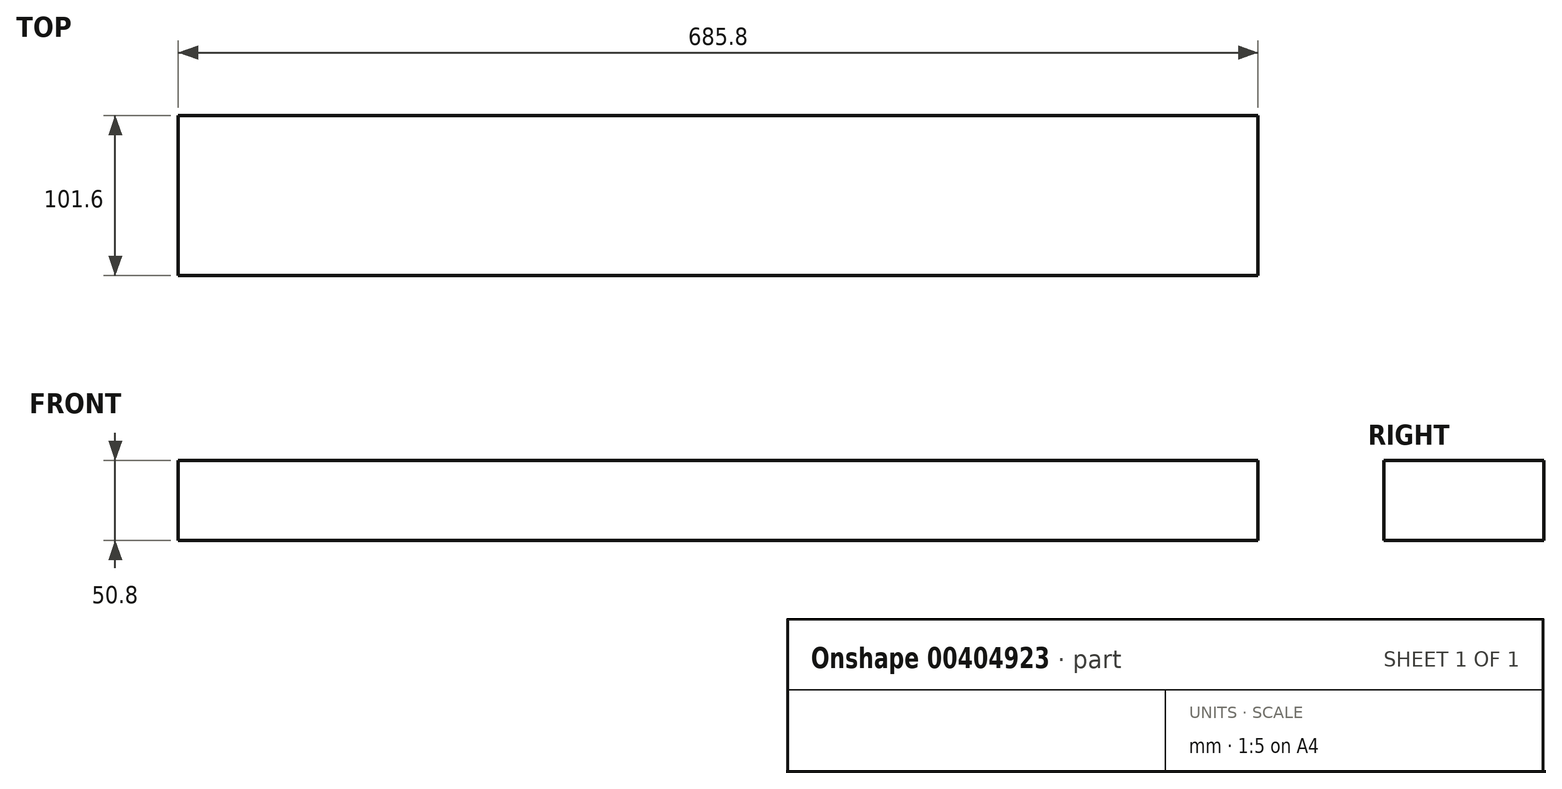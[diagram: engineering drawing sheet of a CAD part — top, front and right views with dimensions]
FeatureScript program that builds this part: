
annotation { "Feature Type Name" : "Feature", "Feature Type Description" : "" }
export const myFeature = defineFeature(function(context is Context, id is Id, definition is map)
    precondition{}
    {
        {
            var Q0;
            Q0=qCreatedBy(makeId("Right.planeOp"),FACE);
            var sketch = newSketch(context, id + "F0", { "sketchPlane" : qUnion([Q0])});
            skLineSegment(sketch, "E0.bottom", {"start": v(0, 0) * mm, "end": v(101.6, 0) * mm});
            skLineSegment(sketch, "E0.top", {"start": v(0, 50.8) * mm, "end": v(101.6, 50.8) * mm});
            skLineSegment(sketch, "E0.left", {"start": v(0, 0) * mm, "end": v(0, 50.8) * mm});
            skLineSegment(sketch, "E0.right", {"start": v(101.6, 0) * mm, "end": v(101.6, 50.8) * mm});
            skSolve(sketch);
        }
        {
            var Q0;
            Q0 = qSketchRegion(id + "F0", true);
            extrude(context, id + "F1", {"entities" : qUnion([Q0]), "depth" : 685.8 * mm});
        }
    });
